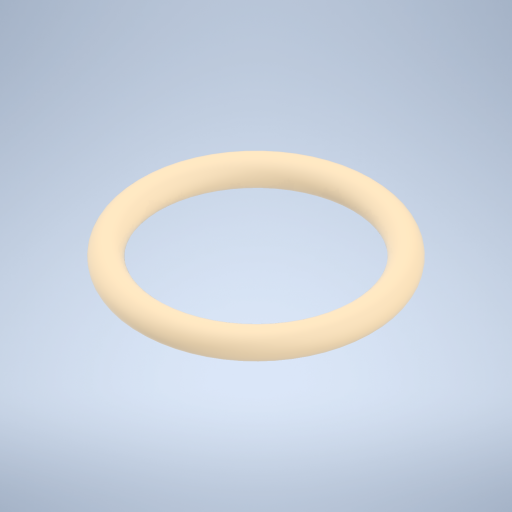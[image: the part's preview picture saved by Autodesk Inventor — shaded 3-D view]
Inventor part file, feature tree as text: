
AUTODESK INVENTOR PART (.ipt)
format: ipt  version: 2024.3 (Build 283343000, 343)  size: 279,040 bytes
history: native  units: mm
features: revolve x1, sketch x1
ambient origin geometry x8: Origin, YZ Plane, XZ Plane, XY Plane, X Axis, Y Axis, Z Axis, Center Point
bodies: Solid1 (feature_tree)
feature tree (2):
  revolve  "Revolution1"  [1 undecoded]
  sketch  "Sketch3"  dims[d3=0.5mm d4=2.0mm d5=90.0deg]
note: 1 required parameter value undecoded (feature->parameter linkage not recoverable at this tier; creation-order binding heuristic only, values carry confidence <= 0.55)
